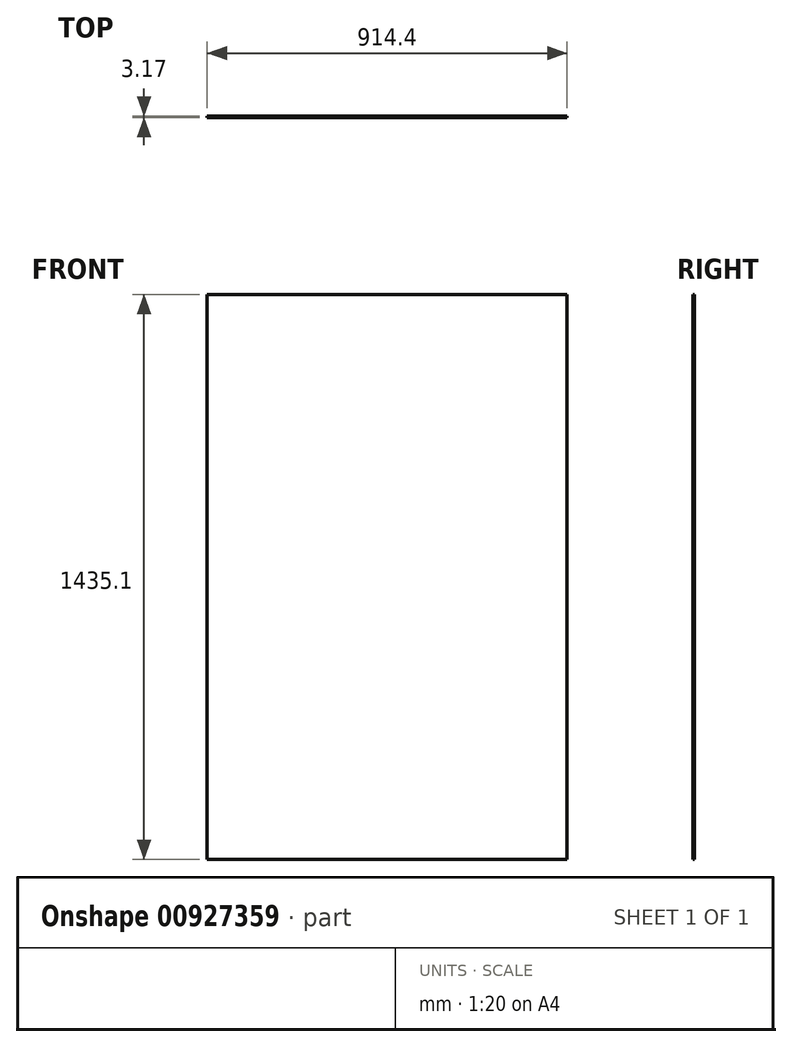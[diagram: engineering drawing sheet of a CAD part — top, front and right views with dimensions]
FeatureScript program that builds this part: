
annotation { "Feature Type Name" : "Feature", "Feature Type Description" : "" }
export const myFeature = defineFeature(function(context is Context, id is Id, definition is map)
    precondition{}
    {
        {
            var Q0;
            Q0=qCreatedBy(makeId("Front.planeOp"),FACE);
            var sketch = newSketch(context, id + "F0", { "sketchPlane" : qUnion([Q0])});
            skLineSegment(sketch, "E0.bottom", {"start": v(-457.2, 717.55) * mm, "end": v(457.2, 717.55) * mm});
            skLineSegment(sketch, "E0.top", {"start": v(-457.2, -717.55) * mm, "end": v(457.2, -717.55) * mm});
            skLineSegment(sketch, "E0.left", {"start": v(-457.2, 717.55) * mm, "end": v(-457.2, -717.55) * mm});
            skLineSegment(sketch, "E0.right", {"start": v(457.2, 717.55) * mm, "end": v(457.2, -717.55) * mm});
            skSolve(sketch);
        }
        {
            var Q0;
            Q0=makeQuery(id+"F0.imprint","IMPRINT",FACE,{"disambiguationData":[TD([[makeQuery(id+"F0.imprint","IMPRINT",EDGE,{"derivedFrom":sQuery(id+"F0.wireOp",EDGE,"E0.bottom")}),-1.0]])]});
            extrude(context, id + "F1", {"entities" : qUnion([Q0]), "depth" : 3.17 * mm, "offsetDistance" : 25.4 * mm});
        }
    });
